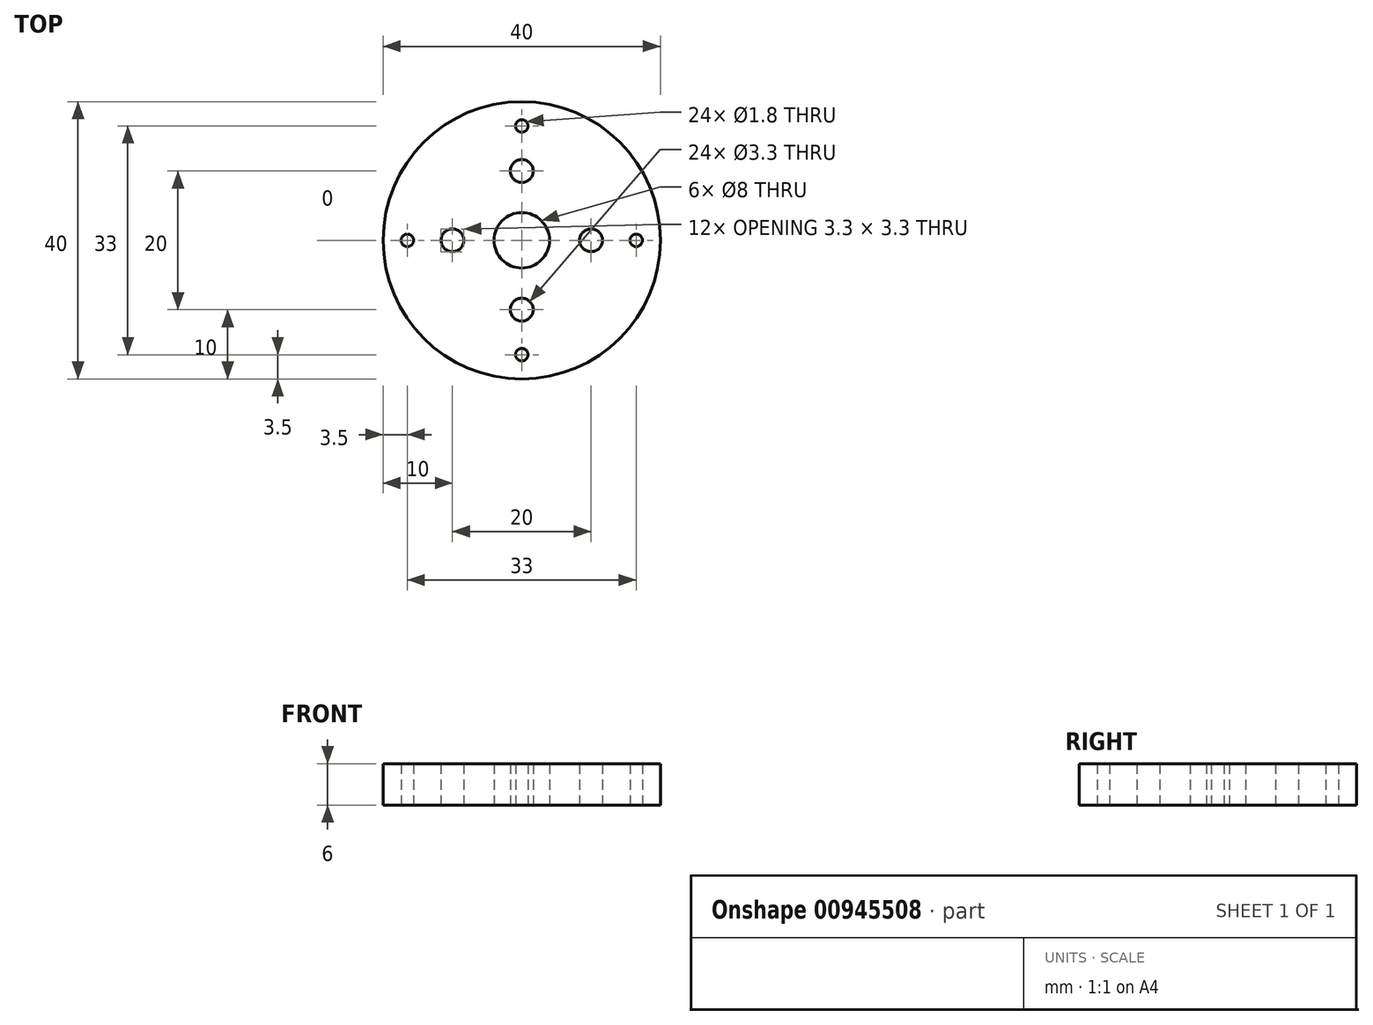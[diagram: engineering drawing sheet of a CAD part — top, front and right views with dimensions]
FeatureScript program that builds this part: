
annotation { "Feature Type Name" : "Feature", "Feature Type Description" : "" }
export const myFeature = defineFeature(function(context is Context, id is Id, definition is map)
    precondition{}
    {
        {
            var Q0;
            Q0=qCreatedBy(makeId("Top.planeOp"),FACE);
            var sketch = newSketch(context, id + "F0", { "sketchPlane" : qUnion([Q0])});
            skCircle(sketch, "E0", {"center": v(0, 0) * mm, "radius": 20 * mm});
            skCircle(sketch, "E1", {"center": v(0, 0) * mm, "radius": 4 * mm});
            skCircle(sketch, "E2", {"center": v(0, 16.5) * mm, "radius": 0.9 * mm});
            skCircle(sketch, "E3", {"center": v(-16.5, 0) * mm, "radius": 0.9 * mm});
            skCircle(sketch, "E4", {"center": v(0, -16.5) * mm, "radius": 0.9 * mm});
            skCircle(sketch, "E5", {"center": v(16.5, 0) * mm, "radius": 0.9 * mm});
            skPoint(sketch, "E6", {"position": v(0, 10) * mm});
            skPoint(sketch, "E7", {"position": v(-10, 0) * mm});
            skPoint(sketch, "E8.MirrorP", {"position": v(10, 0) * mm});
            skPoint(sketch, "E9.MirrorP", {"position": v(0, -10) * mm});
            skSolve(sketch);
        }
        {
            var Q0;
            Q0=makeQuery(id+"F0.imprint","IMPRINT",FACE,{"disambiguationData":[TD([[makeQuery(id+"F0.imprint","IMPRINT",EDGE,{"derivedFrom":sQuery(id+"F0.wireOp",EDGE,"E0")}),1.0]])]});
            extrude(context, id + "F1", {"entities" : qUnion([Q0]), "depth" : 6 * mm, "offsetDistance" : 25 * mm});
        }
        {
            var Q0;
            Q0=sQuery(id+"F0.wireOp",VERTEX,"E7");
            var Q1;
            Q1=sQuery(id+"F0.wireOp",VERTEX,"E6");
            var Q2;
            Q2=sQuery(id+"F0.wireOp",VERTEX,"E8.MirrorP");
            var Q3;
            Q3=sQuery(id+"F0.wireOp",VERTEX,"E9.MirrorP");
            var Q4;
            Q4=makeQuery(id+"F1.opExtrude","SWEPT_BODY",BODY,{"disambiguationData":[OSD([sQuery(id+"F0.wireOp",EDGE,"E0"),sQuery(id+"F0.wireOp",EDGE,"E1"),sQuery(id+"F0.wireOp",EDGE,"E2"),sQuery(id+"F0.wireOp",EDGE,"E3"),sQuery(id+"F0.wireOp",EDGE,"E4"),sQuery(id+"F0.wireOp",EDGE,"E5")])]});
            hole(context, id + "F2", {"style" : HoleStyle.SIMPLE, "endStyle" : HoleEndStyle.THROUGH, "oppositeDirection" : true, "standardTappedOrClearance" : lookupTablePath({ "standard" : "ISO", "engagement" : "75%", "pitch" : "0.7 mm", "size" : "M4", "type" : "Tapped" }), "standardBlindInLast" : lookupTablePath({ "standard" : "ISO", "fit" : "Normal", "engagement" : "75%", "pitch" : "0.7 mm", "size" : "M4", "type" : "Clearance & tapped" }), "holeDiameter" : 3.3 * mm, "majorDiameter" : 4 * mm, "showTappedDepth" : true, "isTappedThrough" : true, "tappedDepth" : 12 * mm, "tapClearance" : 3, "startFromSketch" : true, "locations" : qUnion([Q0, Q1, Q2, Q3]), "scope" : qUnion([Q4])});
        }
    });
